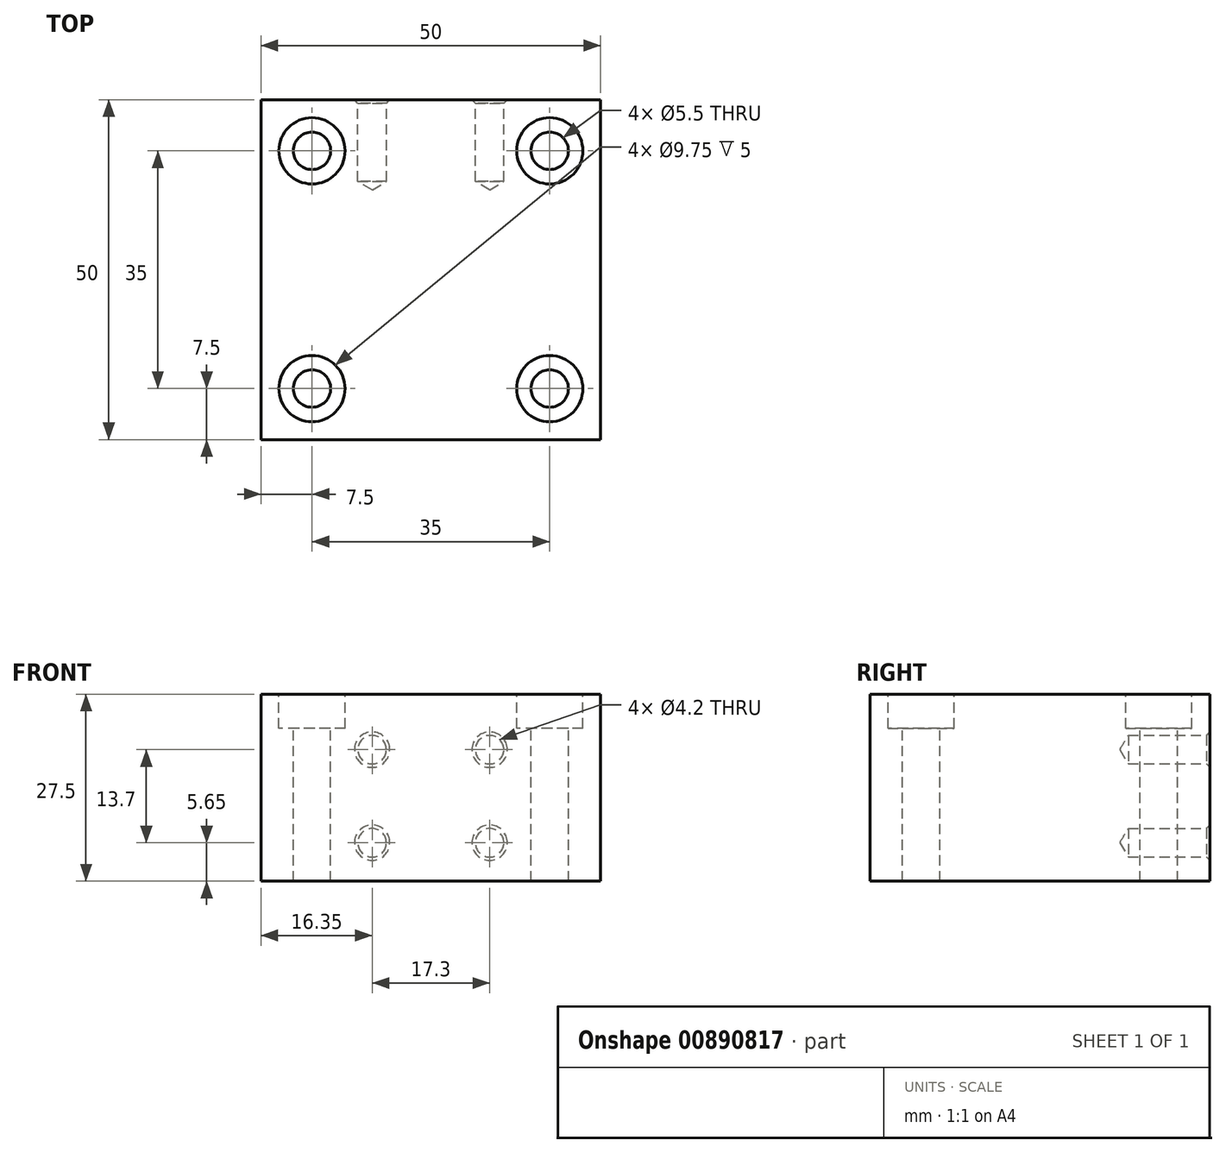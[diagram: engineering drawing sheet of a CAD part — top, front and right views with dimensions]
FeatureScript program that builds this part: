
annotation { "Feature Type Name" : "Feature", "Feature Type Description" : "" }
export const myFeature = defineFeature(function(context is Context, id is Id, definition is map)
    precondition{}
    {
        {
            var Q0;
            Q0=qCreatedBy(makeId("Top.planeOp"),FACE);
            var sketch = newSketch(context, id + "F0", { "sketchPlane" : qUnion([Q0])});
            skLineSegment(sketch, "E0.bottom", {"start": v(-25, 25) * mm, "end": v(25, 25) * mm});
            skLineSegment(sketch, "E0.top", {"start": v(-25, -25) * mm, "end": v(25, -25) * mm});
            skLineSegment(sketch, "E0.left", {"start": v(-25, 25) * mm, "end": v(-25, -25) * mm});
            skLineSegment(sketch, "E0.right", {"start": v(25, 25) * mm, "end": v(25, -25) * mm});
            skPoint(sketch, "E0.middle", {"position": v(0, 0) * mm});
            skSolve(sketch);
        }
        {
            var Q0;
            Q0=makeQuery(id+"F0.imprint","IMPRINT",FACE,{"disambiguationData":[TD([[makeQuery(id+"F0.imprint","IMPRINT",EDGE,{"derivedFrom":sQuery(id+"F0.wireOp",EDGE,"E0.bottom")}),-1.0]])]});
            extrude(context, id + "F1", {"entities" : qUnion([Q0]), "depth" : 27.5 * mm, "offsetDistance" : 25 * mm});
        }
        {
            var Q0;
            Q0=makeQuery(id+"F1.opExtrude","CAP_FACE",FACE,{"disambiguationData":[OSD([sQuery(id+"F0.wireOp",EDGE,"E0.bottom"),sQuery(id+"F0.wireOp",EDGE,"E0.top"),sQuery(id+"F0.wireOp",EDGE,"E0.left"),sQuery(id+"F0.wireOp",EDGE,"E0.right")])],"isStart":false});
            var sketch = newSketch(context, id + "F2", { "sketchPlane" : qUnion([Q0])});
            skLineSegment(sketch, "E1", {"start": v(0, 27.41) * mm, "end": v(0, -29.08) * mm, "construction": true});
            skPoint(sketch, "E1.startSnap0", {"position": v(0, 25) * mm});
            skLineSegment(sketch, "E2", {"start": v(-27.3, 0) * mm, "end": v(27.83, 0) * mm, "construction": true});
            skLineSegment(sketch, "E3", {"start": v(-17.5, 27.41) * mm, "end": v(-17.5, -29.08) * mm, "construction": true});
            skLineSegment(sketch, "E4", {"start": v(17.5, 27.73) * mm, "end": v(17.5, -27.93) * mm, "construction": true});
            skLineSegment(sketch, "E5", {"start": v(-28.03, 17.5) * mm, "end": v(27.83, 17.5) * mm, "construction": true});
            skLineSegment(sketch, "E6", {"start": v(-27.2, -17.5) * mm, "end": v(29.72, -17.5) * mm, "construction": true});
            skPoint(sketch, "E7", {"position": v(-17.5, 17.5) * mm});
            skPoint(sketch, "E8", {"position": v(17.5, 17.5) * mm});
            skPoint(sketch, "E9", {"position": v(17.5, -17.5) * mm});
            skPoint(sketch, "E10", {"position": v(-17.5, -17.5) * mm});
            skSolve(sketch);
        }
        {
            var Q0;
            Q0=sQuery(id+"F2.wireOp",VERTEX,"E7");
            var Q1;
            Q1=sQuery(id+"F2.wireOp",VERTEX,"E8");
            var Q2;
            Q2=sQuery(id+"F2.wireOp",VERTEX,"E10");
            var Q3;
            Q3=sQuery(id+"F2.wireOp",VERTEX,"E9");
            var Q4;
            Q4=makeQuery(id+"F1.opExtrude","SWEPT_BODY",BODY,{"disambiguationData":[OSD([sQuery(id+"F0.wireOp",EDGE,"E0.bottom"),sQuery(id+"F0.wireOp",EDGE,"E0.top"),sQuery(id+"F0.wireOp",EDGE,"E0.left"),sQuery(id+"F0.wireOp",EDGE,"E0.right")])]});
            hole(context, id + "F3", {"style" : HoleStyle.C_BORE, "endStyle" : HoleEndStyle.THROUGH, "standardTappedOrClearance" : lookupTablePath({ "fit" : "Normal", "standard" : "ISO", "size" : "M5", "type" : "Clearance" }), "standardBlindInLast" : lookupTablePath({ "fit" : "Normal", "standard" : "ISO", "size" : "M5", "type" : "Clearance" }), "holeDiameter" : 5.5 * mm, "cBoreDiameter" : 9.75 * mm, "cBoreDepth" : 5 * mm, "majorDiameter" : 5 * mm, "isTappedThrough" : true, "tappedDepth" : 12 * mm, "tapClearance" : 3, "locations" : qUnion([Q0, Q1, Q2, Q3]), "scope" : qUnion([Q4])});
        }
        {
            var Q0;
            Q0=makeQuery(id+"F1.opExtrude","SWEPT_FACE",FACE,{"disambiguationData":[OSD([sQuery(id+"F0.wireOp",EDGE,"E0.bottom")])]});
            var sketch = newSketch(context, id + "F4", { "sketchPlane" : qUnion([Q0])});
            skLineSegment(sketch, "E11", {"start": v(-24.24, 12.5) * mm, "end": v(24.9, 12.5) * mm, "construction": true});
            skLineSegment(sketch, "E12", {"start": v(0, 29.37) * mm, "end": v(0, -2.38) * mm, "construction": true});
            skPoint(sketch, "E12.startSnap0", {"position": v(0, 27.5) * mm});
            skLineSegment(sketch, "E13", {"start": v(-8.65, 30.12) * mm, "end": v(-8.65, -2.38) * mm, "construction": true});
            skLineSegment(sketch, "E14", {"start": v(8.65, 29.98) * mm, "end": v(8.65, -2.38) * mm, "construction": true});
            skLineSegment(sketch, "E15", {"start": v(-13.74, 19.35) * mm, "end": v(11.51, 19.35) * mm, "construction": true});
            skLineSegment(sketch, "E16", {"start": v(-14.49, 5.65) * mm, "end": v(12.95, 5.65) * mm, "construction": true});
            skPoint(sketch, "E17", {"position": v(-8.65, 19.35) * mm});
            skPoint(sketch, "E18", {"position": v(8.65, 19.35) * mm});
            skPoint(sketch, "E19", {"position": v(8.65, 5.65) * mm});
            skPoint(sketch, "E20", {"position": v(-8.65, 5.65) * mm});
            skSolve(sketch);
        }
        {
            var Q0;
            Q0=sQuery(id+"F4.wireOp",VERTEX,"E17");
            var Q1;
            Q1=sQuery(id+"F4.wireOp",VERTEX,"E18");
            var Q2;
            Q2=sQuery(id+"F4.wireOp",VERTEX,"E19");
            var Q3;
            Q3=sQuery(id+"F4.wireOp",VERTEX,"E20");
            var Q4;
            Q4=makeQuery(id+"F1.opExtrude","SWEPT_BODY",BODY,{"disambiguationData":[OSD([sQuery(id+"F0.wireOp",EDGE,"E0.bottom"),sQuery(id+"F0.wireOp",EDGE,"E0.top"),sQuery(id+"F0.wireOp",EDGE,"E0.left"),sQuery(id+"F0.wireOp",EDGE,"E0.right")])]});
            hole(context, id + "F5", {"style" : HoleStyle.C_SINK, "endStyle" : HoleEndStyle.BLIND, "holeDiameter" : 4.2 * mm, "cSinkDiameter" : 5.2 * mm, "cSinkAngle" : 90 * degree, "majorDiameter" : 5 * mm, "holeDepth" : 12 * mm, "isTappedThrough" : true, "tappedDepth" : 12 * mm, "tapClearance" : 3, "locations" : qUnion([Q0, Q1, Q2, Q3]), "scope" : qUnion([Q4])});
        }
    });
